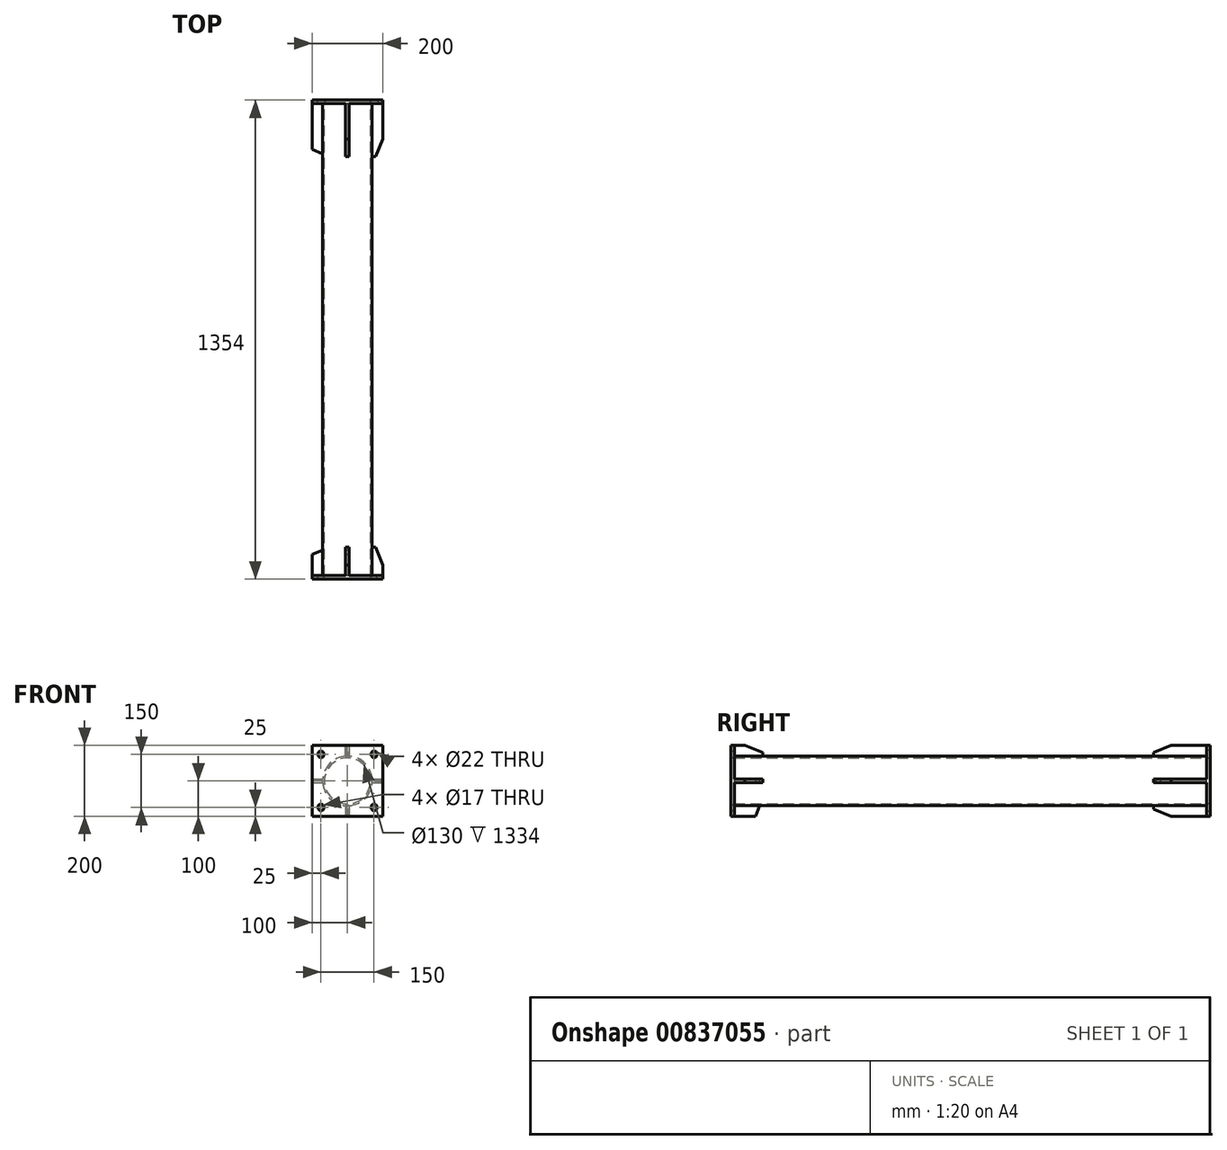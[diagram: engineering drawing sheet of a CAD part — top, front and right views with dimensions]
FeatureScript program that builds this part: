
annotation { "Feature Type Name" : "Feature", "Feature Type Description" : "" }
export const myFeature = defineFeature(function(context is Context, id is Id, definition is map)
    precondition{}
    {
        {
            var Q0;
            Q0=qCreatedBy(makeId("Front.planeOp"),FACE);
            var sketch = newSketch(context, id + "F0", { "sketchPlane" : qUnion([Q0])});
            skCircle(sketch, "E0", {"center": v(0, 0) * mm, "radius": 70 * mm});
            skCircle(sketch, "E1", {"center": v(0, 0) * mm, "radius": 65 * mm});
            skSolve(sketch);
        }
        {
            var Q0;
            Q0=qSketchRegion(id+"F0",true);
            extrude(context, id + "F1", {"entities" : qUnion([Q0]), "depth" : 1334 * mm, "offsetDistance" : 25 * mm});
        }
        {
            var Q0;
            Q0=qCreatedBy(makeId("Front.planeOp"),FACE);
            var sketch = newSketch(context, id + "F2", { "sketchPlane" : qUnion([Q0])});
            skLineSegment(sketch, "E2.bottom", {"start": v(-100, 100) * mm, "end": v(100, 100) * mm});
            skLineSegment(sketch, "E2.top", {"start": v(-100, -100) * mm, "end": v(100, -100) * mm});
            skLineSegment(sketch, "E2.left", {"start": v(-100, 100) * mm, "end": v(-100, -100) * mm});
            skLineSegment(sketch, "E2.right", {"start": v(100, 100) * mm, "end": v(100, -100) * mm});
            skLineSegment(sketch, "E3", {"start": v(-100, 0) * mm, "end": v(100, 0) * mm, "construction": true});
            skLineSegment(sketch, "E4", {"start": v(0, 100) * mm, "end": v(0, -100) * mm, "construction": true});
            skCircle(sketch, "E5", {"center": v(-75, 75) * mm, "radius": 11 * mm});
            skCircle(sketch, "E6.MirrorC", {"center": v(-75, -75) * mm, "radius": 11 * mm});
            skCircle(sketch, "E7.MirrorC", {"center": v(75, 75) * mm, "radius": 11 * mm});
            skCircle(sketch, "E8.MirrorC", {"center": v(75, -75) * mm, "radius": 11 * mm});
            skSolve(sketch);
        }
        {
            var Q0;
            Q0=qSketchRegion(id+"F2",true);
            extrude(context, id + "F3", {"entities" : qUnion([Q0]), "operationType" : NewBodyOperationType.ADD, "oppositeDirection" : true, "depth" : 10 * mm, "offsetDistance" : 25 * mm});
        }
        {
            var Q0;
            Q0=qCreatedBy(makeId("Front.planeOp"),FACE);
            var sketch = newSketch(context, id + "F4", { "sketchPlane" : qUnion([Q0])});
            skLineSegment(sketch, "E9.bottom", {"start": v(-100, 5) * mm, "end": v(-69.82, 5) * mm});
            skLineSegment(sketch, "E9.top", {"start": v(-100, -5) * mm, "end": v(-69.82, -5) * mm});
            skLineSegment(sketch, "E9.left", {"start": v(-100, 5) * mm, "end": v(-100, -5) * mm});
            skLineSegment(sketch, "E9.right", {"start": v(-69.82, 5) * mm, "end": v(-69.82, -5) * mm});
            skLineSegment(sketch, "E10.bottom", {"start": v(-5, 69.82) * mm, "end": v(5, 69.82) * mm});
            skLineSegment(sketch, "E10.top", {"start": v(-5, 100) * mm, "end": v(5, 100) * mm});
            skLineSegment(sketch, "E10.left", {"start": v(-5, 69.82) * mm, "end": v(-5, 100) * mm});
            skLineSegment(sketch, "E10.right", {"start": v(5, 69.82) * mm, "end": v(5, 100) * mm});
            skLineSegment(sketch, "E11.bottom", {"start": v(69.82, 5) * mm, "end": v(100, 5) * mm});
            skLineSegment(sketch, "E11.top", {"start": v(69.82, -5) * mm, "end": v(100, -5) * mm});
            skLineSegment(sketch, "E11.left", {"start": v(69.82, 5) * mm, "end": v(69.82, -5) * mm});
            skLineSegment(sketch, "E11.right", {"start": v(100, 5) * mm, "end": v(100, -5) * mm});
            skLineSegment(sketch, "E12.bottom", {"start": v(5, -69.82) * mm, "end": v(-5, -69.82) * mm});
            skLineSegment(sketch, "E12.top", {"start": v(5, -100) * mm, "end": v(-5, -100) * mm});
            skLineSegment(sketch, "E12.left", {"start": v(5, -69.82) * mm, "end": v(5, -100) * mm});
            skLineSegment(sketch, "E12.right", {"start": v(-5, -69.82) * mm, "end": v(-5, -100) * mm});
            skSolve(sketch);
        }
        {
            var Q0;
            Q0=qSketchRegion(id+"F4",true);
            extrude(context, id + "F5", {"entities" : qUnion([Q0]), "operationType" : NewBodyOperationType.ADD, "depth" : 150 * mm, "offsetDistance" : 25 * mm});
        }
        {
            var Q0;
            Q0=makeQuery(id+"F5.opExtrude","CAP_EDGE",EDGE,{"disambiguationData":[OSD([sQuery(id+"F4.wireOp",EDGE,"E9.left")])],"isStart":false});
            var Q1;
            Q1=makeQuery(id+"F5.opExtrude","CAP_EDGE",EDGE,{"disambiguationData":[OSD([sQuery(id+"F4.wireOp",EDGE,"E10.top")])],"isStart":false});
            var Q2;
            Q2=makeQuery(id+"F5.opExtrude","CAP_EDGE",EDGE,{"disambiguationData":[OSD([sQuery(id+"F4.wireOp",EDGE,"E12.top")])],"isStart":false});
            var Q3;
            Q3=makeQuery(id+"F5.opExtrude","CAP_EDGE",EDGE,{"disambiguationData":[OSD([sQuery(id+"F4.wireOp",EDGE,"E11.right")])],"isStart":false});
            chamfer(context, id + "F6", {"entities" : qUnion([Q0, Q1, Q2, Q3]), "chamferType" : ChamferType.TWO_OFFSETS, "width1" : 50 * mm, "oppositeDirection" : false, "width2" : 20 * mm});
        }
        {
            var Q0;
            Q0=makeQuery(id+"F1.opExtrude","CAP_FACE",FACE,{"disambiguationData":[OSD([sQuery(id+"F0.wireOp",EDGE,"E0"),sQuery(id+"F0.wireOp",EDGE,"E1")])],"isStart":false});
            cPlane(context, id + "F7", {"entities" : qUnion([Q0]), "cplaneType" : CPlaneType.OFFSET, "offset" : 0 * mm, "width" : 150 * mm, "height" : 150 * mm});
        }
        {
            var Q0;
            Q0=qCreatedBy(id+"F7.planeOp",FACE);
            var sketch = newSketch(context, id + "F8", { "sketchPlane" : qUnion([Q0])});
            skLineSegment(sketch, "E13.bottom", {"start": v(-100, 100) * mm, "end": v(100, 100) * mm});
            skLineSegment(sketch, "E13.top", {"start": v(-100, -100) * mm, "end": v(100, -100) * mm});
            skLineSegment(sketch, "E13.left", {"start": v(-100, 100) * mm, "end": v(-100, -100) * mm});
            skLineSegment(sketch, "E13.right", {"start": v(100, 100) * mm, "end": v(100, -100) * mm});
            skCircle(sketch, "E14", {"center": v(-75, 75) * mm, "radius": 8.5 * mm});
            skCircle(sketch, "E15.MirrorC", {"center": v(75, 75) * mm, "radius": 8.5 * mm});
            skLineSegment(sketch, "E16", {"start": v(-100, 0) * mm, "end": v(100, 0) * mm, "construction": true});
            skLineSegment(sketch, "E17", {"start": v(0, 100) * mm, "end": v(0, -100) * mm, "construction": true});
            skCircle(sketch, "E18.MirrorC", {"center": v(-75, -75) * mm, "radius": 8.5 * mm});
            skCircle(sketch, "E19.MirrorC", {"center": v(75, -75) * mm, "radius": 8.5 * mm});
            skSolve(sketch);
        }
        {
            var Q0;
            Q0=qSketchRegion(id+"F8",true);
            extrude(context, id + "F9", {"entities" : qUnion([Q0]), "operationType" : NewBodyOperationType.ADD, "depth" : 10 * mm, "offsetDistance" : 25 * mm});
        }
        {
            var Q0;
            {var subQ0=sQuery(id+"F8.wireOp",EDGE,"E13.left");var subQ1=sQuery(id+"F8.wireOp",EDGE,"E13.top");var subQ2=sQuery(id+"F8.wireOp",EDGE,"E13.bottom");var subQ3=sQuery(id+"F8.wireOp",EDGE,"E13.right");var subQ4=sQuery(id+"F8.wireOp",EDGE,"E14");var subQ5=sQuery(id+"F8.wireOp",EDGE,"E15.MirrorC");var subQ6=sQuery(id+"F8.wireOp",EDGE,"E18.MirrorC");var subQ7=sQuery(id+"F8.wireOp",EDGE,"E19.MirrorC");Q0=makeQuery(id+"F9.boolean.opBoolean","SPLIT",FACE,{"disambiguationData":[TD([makeQuery(id+"F1.opExtrude","SWEPT_FACE",FACE,{"disambiguationData":[OSD([sQuery(id+"F0.wireOp",EDGE,"E0")])]})])],"derivedFrom":makeQuery(id+"F9.opExtrude","CAP_FACE",FACE,{"disambiguationData":[OSD([subQ2,subQ1,subQ0,subQ3,subQ4,subQ5,subQ6,subQ7])],"isStart":true})});}
            var sketch = newSketch(context, id + "F10", { "sketchPlane" : qUnion([Q0])});
            skLineSegment(sketch, "E20.bottom", {"start": v(5, 100) * mm, "end": v(-5, 100) * mm});
            skLineSegment(sketch, "E20.top", {"start": v(5, 69.82) * mm, "end": v(-5, 69.82) * mm});
            skLineSegment(sketch, "E20.left", {"start": v(5, 100) * mm, "end": v(5, 69.82) * mm});
            skLineSegment(sketch, "E20.right", {"start": v(-5, 100) * mm, "end": v(-5, 69.82) * mm});
            skLineSegment(sketch, "E21.bottom", {"start": v(100, 5) * mm, "end": v(69.82, 5) * mm});
            skLineSegment(sketch, "E21.top", {"start": v(100, -5) * mm, "end": v(69.82, -5) * mm});
            skLineSegment(sketch, "E21.left", {"start": v(100, 5) * mm, "end": v(100, -5) * mm});
            skLineSegment(sketch, "E21.right", {"start": v(69.82, 5) * mm, "end": v(69.82, -5) * mm});
            skLineSegment(sketch, "E22.bottom", {"start": v(-5, -69.82) * mm, "end": v(5, -69.82) * mm});
            skLineSegment(sketch, "E22.top", {"start": v(-5, -100) * mm, "end": v(5, -100) * mm});
            skLineSegment(sketch, "E22.left", {"start": v(-5, -69.82) * mm, "end": v(-5, -100) * mm});
            skLineSegment(sketch, "E22.right", {"start": v(5, -69.82) * mm, "end": v(5, -100) * mm});
            skLineSegment(sketch, "E23.bottom", {"start": v(-69.82, -5) * mm, "end": v(-100, -5) * mm});
            skLineSegment(sketch, "E23.top", {"start": v(-69.82, 5) * mm, "end": v(-100, 5) * mm});
            skLineSegment(sketch, "E23.left", {"start": v(-69.82, -5) * mm, "end": v(-69.82, 5) * mm});
            skLineSegment(sketch, "E23.right", {"start": v(-100, -5) * mm, "end": v(-100, 5) * mm});
            skSolve(sketch);
        }
        {
            var Q0;
            Q0 = qSketchRegion(id + "F10", true);
            extrude(context, id + "F11", {"entities" : qUnion([Q0]), "operationType" : NewBodyOperationType.ADD, "depth" : 80 * mm, "offsetDistance" : 25 * mm});
        }
        {
            var Q0;
            Q0=makeQuery(id+"F11.opExtrude","CAP_EDGE",EDGE,{"disambiguationData":[OSD([sQuery(id+"F10.wireOp",EDGE,"E21.left")])],"isStart":false});
            var Q1;
            Q1=makeQuery(id+"F11.opExtrude","CAP_EDGE",EDGE,{"disambiguationData":[OSD([sQuery(id+"F10.wireOp",EDGE,"E22.top")])],"isStart":false});
            var Q2;
            Q2=makeQuery(id+"F11.opExtrude","CAP_EDGE",EDGE,{"disambiguationData":[OSD([sQuery(id+"F10.wireOp",EDGE,"E20.bottom")])],"isStart":false});
            var Q3;
            Q3=makeQuery(id+"F11.opExtrude","CAP_EDGE",EDGE,{"disambiguationData":[OSD([sQuery(id+"F10.wireOp",EDGE,"E23.right")])],"isStart":false});
            chamfer(context, id + "F12", {"entities" : qUnion([Q0, Q1, Q2, Q3]), "chamferType" : ChamferType.TWO_OFFSETS, "width1" : 20 * mm, "oppositeDirection" : false, "width2" : 50 * mm});
        }
    });
